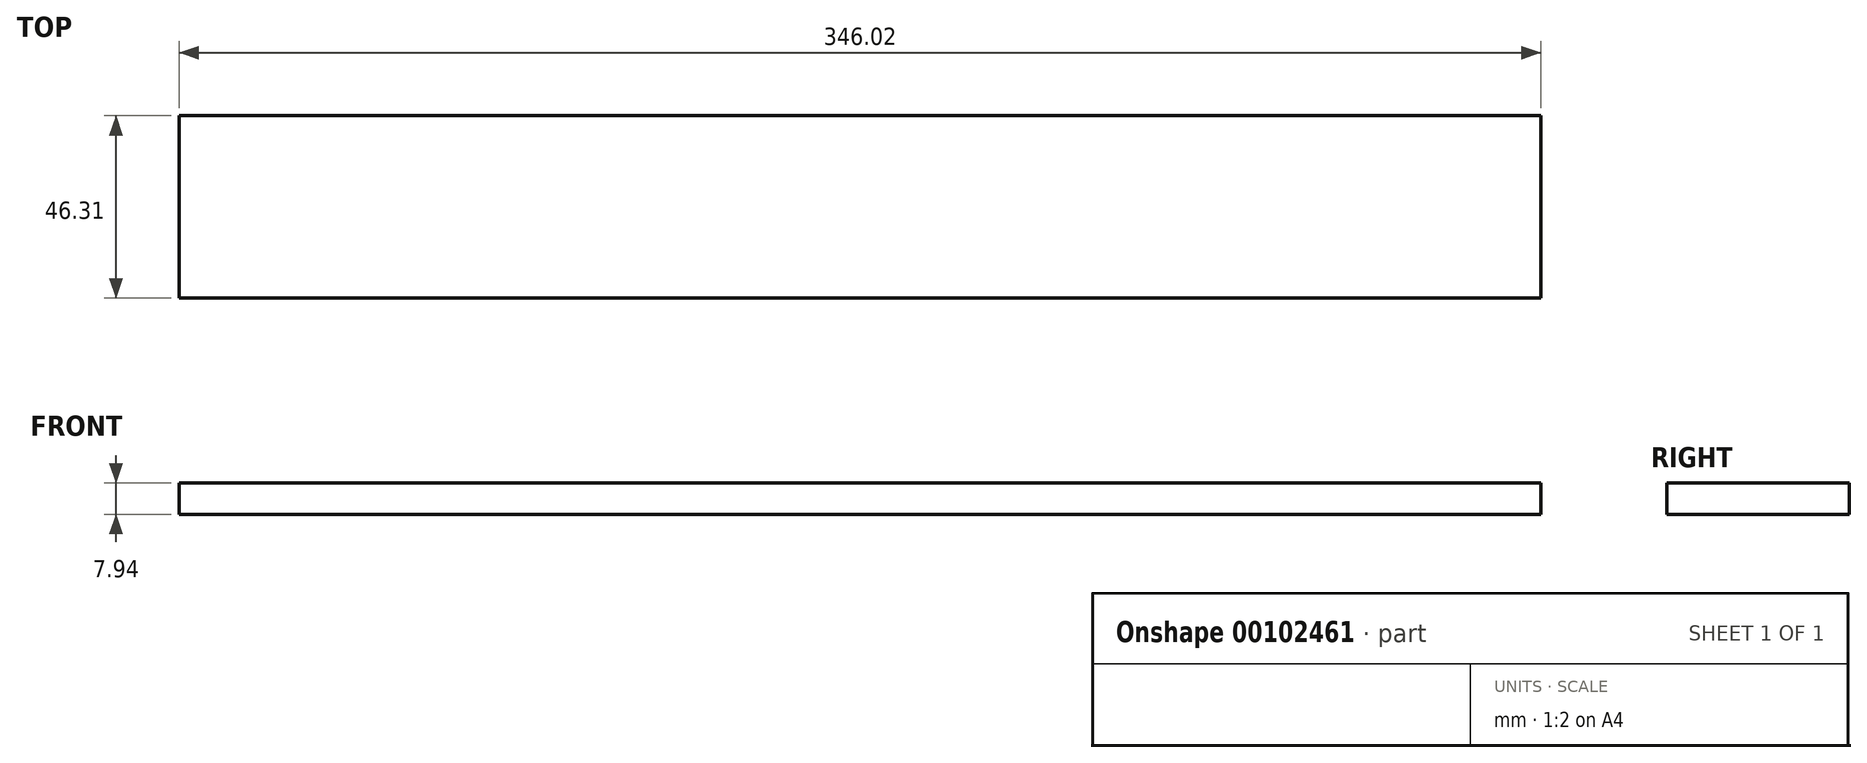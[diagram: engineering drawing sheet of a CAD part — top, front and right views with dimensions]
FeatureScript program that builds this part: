
annotation { "Feature Type Name" : "Feature", "Feature Type Description" : "" }
export const myFeature = defineFeature(function(context is Context, id is Id, definition is map)
    precondition{}
    {
        {
            var Q0;
            Q0=qCreatedBy(makeId("Top.planeOp"),FACE);
            var sketch = newSketch(context, id + "F0", { "sketchPlane" : qUnion([Q0])});
            skLineSegment(sketch, "E0.bottom", {"start": v(0, 0) * mm, "end": v(346.02, 0) * mm});
            skLineSegment(sketch, "E0.top", {"start": v(0, 46.31) * mm, "end": v(346.02, 46.31) * mm});
            skLineSegment(sketch, "E0.left", {"start": v(0, 0) * mm, "end": v(0, 46.31) * mm});
            skLineSegment(sketch, "E0.right", {"start": v(346.02, 0) * mm, "end": v(346.02, 46.31) * mm});
            skSolve(sketch);
        }
        {
            var Q0;
            Q0 = qSketchRegion(id + "F0", true);
            extrude(context, id + "F1", {"entities" : qUnion([Q0]), "depth" : 7.94 * mm});
        }
    });
